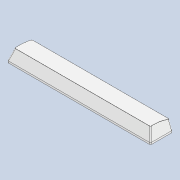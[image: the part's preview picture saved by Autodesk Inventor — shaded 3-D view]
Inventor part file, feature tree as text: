
AUTODESK INVENTOR PART (.ipt)
format: ipt  version: 2021 (Build 250183000, 183)  size: 273,408 bytes
history: native  units: in
note: dims shown in document units (in); Inventor stores cm internally (conversion verified against a paired STEP export)
features: sketch x1
ambient origin geometry x8: Origin, YZ Plane, XZ Plane, XY Plane, X Axis, Y Axis, Z Axis, Center Point
bodies: Solid1 (feature_tree)
feature tree (1):
  sketch  "Sketch-Pattern1"
